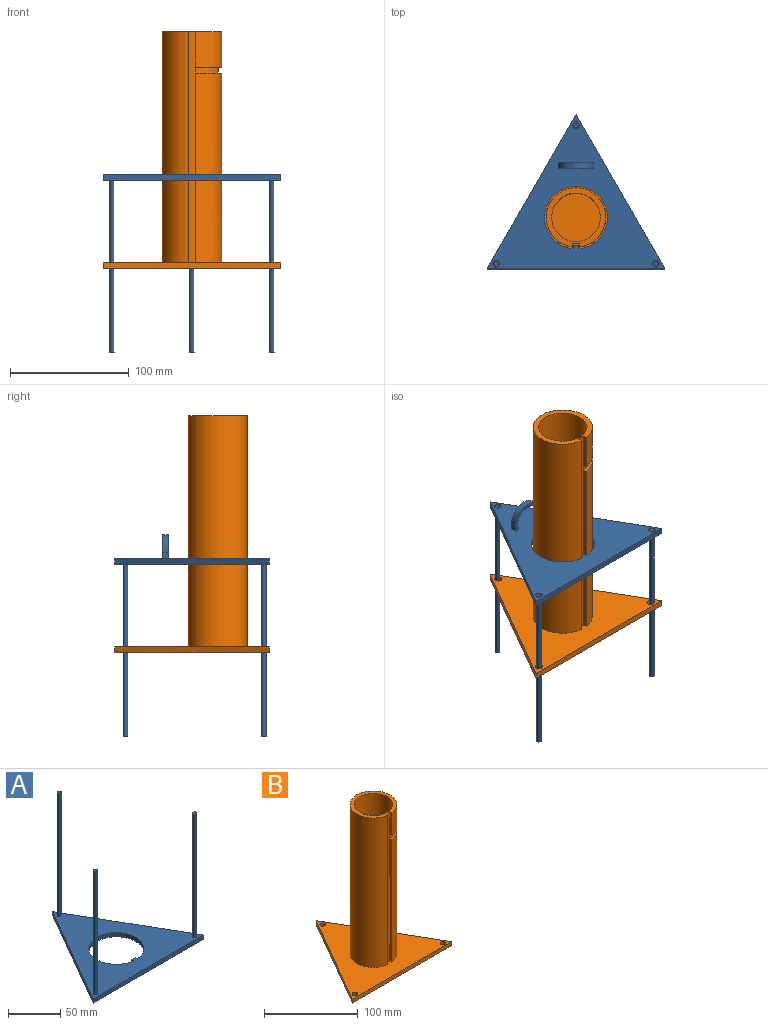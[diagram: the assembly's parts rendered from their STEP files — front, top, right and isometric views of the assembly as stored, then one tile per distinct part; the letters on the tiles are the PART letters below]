
ASSEMBLY  parts=2 mates=2
PART A: 49 faces, bbox 150x129.9x170 mm
  f0: plane 150x129.9mm, normal (0,0,-1), area 7430.6mm2, adj f1,f2,f3,f4,f5,f6,f7,f8
  f1: plane 30x20mm, normal (0,-1,0), area 159mm2, adj f0,f11,f12,f13,f14,f15
  f2: plane 30x20mm, normal (0,1,0), area 159mm2, adj f0,f11,f12,f13,f14,f15
  f3: plane 129.9x75mm, normal (0.87,0.5,0), area 750mm2, adj f0,f4,f8,f10
  f4: plane 129.9x75mm, normal (-0.87,0.5,0), area 750mm2, adj f0,f3,f8,f10
  f5: cylinder r=26.5mm len=53mm, axis (0,0,-1), area 807.5mm2, adj f0,f6,f9,f10
  f6: plane 5x2.7mm, normal (1,0,0), area 13.5mm2, adj f0,f5,f7,f10
  f7: plane 5x5mm, normal (0,1,0), area 25mm2, adj f0,f6,f9,f10
  f8: plane 150x5mm, normal (0,-1,0), area 750mm2, adj f0,f3,f4,f10
  f9: plane 5x2.7mm, normal (-1,0,0), area 13.5mm2, adj f0,f5,f7,f10
  f10: plane 150x129.9mm, normal (0,0,1), area 7512.8mm2, adj f3,f4,f5,f6,f7,f8,f9,f39
  f11: plane 5x5mm, normal (-1,0,0), area 25mm2, adj f0,f1,f2,f15
  f12: plane 5x5mm, normal (1,0,0), area 25mm2, adj f0,f1,f2,f15
  f13: plane 5x5mm, normal (1,0,0), area 25mm2, adj f0,f1,f2,f14
  f14: cylinder r=12mm len=24mm, axis (0,1,0), area 214.3mm2, adj f0,f1,f2,f13
  f15: cylinder r=15mm len=30mm, axis (0,1,0), area 235.6mm2, adj f1,f2,f11,f12
  f16: plane 2.85x2.6mm, normal (0.87,-0.5,0), area 8.6mm2, adj f0,f17,f21,f22
  f17: plane 2.85x2.6mm, normal (0.87,0.5,0), area 8.6mm2, adj f0,f16,f18,f22
  f18: plane 3.29x2.6mm, normal (0,1,0), area 8.6mm2, adj f0,f17,f19,f22
  f19: plane 2.85x2.6mm, normal (-0.87,0.5,0), area 8.6mm2, adj f0,f18,f20,f22
  f20: plane 2.85x2.6mm, normal (-0.87,-0.5,0), area 8.6mm2, adj f0,f19,f21,f22
  f21: plane 3.29x2.6mm, normal (0,-1,0), area 8.6mm2, adj f0,f16,f20,f22
  f22: plane 6.58x5.7mm, normal (0,0,-1), area 15.6mm2, adj f16,f17,f18,f19,f20,f21,f38
  f23: plane 2.85x2.6mm, normal (0.87,-0.5,0), area 8.6mm2, adj f0,f24,f28,f29
  f24: plane 2.85x2.6mm, normal (0.87,0.5,0), area 8.6mm2, adj f0,f23,f25,f29
  f25: plane 3.29x2.6mm, normal (0,1,0), area 8.6mm2, adj f0,f24,f26,f29
  f26: plane 2.85x2.6mm, normal (-0.87,0.5,0), area 8.6mm2, adj f0,f25,f27,f29
  f27: plane 2.85x2.6mm, normal (-0.87,-0.5,0), area 8.6mm2, adj f0,f26,f28,f29
  f28: plane 3.29x2.6mm, normal (0,-1,0), area 8.6mm2, adj f0,f23,f27,f29
  f29: plane 6.58x5.7mm, normal (0,0,-1), area 15.6mm2, adj f23,f24,f25,f26,f27,f28,f46
  f30: plane 2.85x2.6mm, normal (0.87,-0.5,0), area 8.6mm2, adj f0,f31,f35,f36
  f31: plane 2.85x2.6mm, normal (0.87,0.5,0), area 8.6mm2, adj f0,f30,f32,f36
  f32: plane 3.29x2.6mm, normal (0,1,0), area 8.6mm2, adj f0,f31,f33,f36
  f33: plane 2.85x2.6mm, normal (-0.87,0.5,0), area 8.6mm2, adj f0,f32,f34,f36
  f34: plane 2.85x2.6mm, normal (-0.87,-0.5,0), area 8.6mm2, adj f0,f33,f35,f36
  f35: plane 3.29x2.6mm, normal (0,-1,0), area 8.6mm2, adj f0,f30,f34,f36
  f36: plane 6.58x5.7mm, normal (0,0,-1), area 15.6mm2, adj f30,f31,f32,f33,f34,f35,f42
  f37: plane 4x4mm, normal (0,0,-1), area 12.6mm2, adj f38
  f38: cylinder r=2mm len=4mm, axis (0,0,-1), area 32.7mm2, adj f22,f37
  f39: cylinder r=2mm len=145mm, axis (0,0,-1), area 1822.1mm2, adj f10,f40
  f40: plane 4x4mm, normal (0,0,1), area 12.6mm2, adj f39
  f41: plane 4x4mm, normal (0,0,-1), area 12.6mm2, adj f42
  f42: cylinder r=2mm len=4mm, axis (0,0,-1), area 32.7mm2, adj f36,f41
  f43: cylinder r=2mm len=145mm, axis (0,0,-1), area 1822.1mm2, adj f10,f44
  f44: plane 4x4mm, normal (0,0,1), area 12.6mm2, adj f43
  f45: plane 4x4mm, normal (0,0,-1), area 12.6mm2, adj f46
  f46: cylinder r=2mm len=4mm, axis (0,0,-1), area 32.7mm2, adj f29,f45
  f47: cylinder r=2mm len=145mm, axis (0,0,-1), area 1822.1mm2, adj f10,f48
  f48: plane 4x4mm, normal (0,0,1), area 12.6mm2, adj f47
PART B: 25 faces, bbox 150x129.9x200 mm
  f0: plane 35.13x22.19mm, normal (0,0,1), area 131.2mm2, adj f1,f2,f3,f4,f5,f6
  f1: plane 20x2.57mm, normal (-0.51,0.86,0), area 59.7mm2, adj f0,f2,f6,f7
  f2: plane 25x4.72mm, normal (0.86,0.51,0), area 135.6mm2, adj f0,f1,f3,f7,f8,f9,f10
  f3: cylinder r=22mm len=30.85mm, axis (0,0,-1), area 205.2mm2, adj f0,f2,f4,f11
  f4: plane 195x6mm, normal (0,-1,0), area 1169.1mm2, adj f0,f3,f5,f11,f12,f13,f14,f15
  f5: plane 160x3mm, normal (-1,0,0), area 480mm2, adj f0,f4,f6,f15
  f6: cylinder r=25mm len=195mm, axis (0,0,-1), area 28838.8mm2, adj f0,f1,f5,f7,f8,f11,f12,f13
  f7: plane 6.26x5.38mm, normal (0,0,1), area 17mm2, adj f1,f2,f6,f8
  f8: plane 25x2.58mm, normal (0.51,-0.86,0), area 67.2mm2, adj f2,f6,f7,f9,f11
  f9: plane 1.94x1.36mm, normal (0.43,-0.56,-0.71), area 0.4mm2, adj f2,f8,f10,f11
  f10: cone r=17mm half-angle=45deg, axis (0,0,1), area 0.7mm2, adj f2,f9,f11
  f11: plane 39.86x22.19mm, normal (0,0,-1), area 147.5mm2, adj f3,f4,f6,f8,f9,f10,f12
  f12: plane 30x3mm, normal (-1,0,0), area 90mm2, adj f4,f6,f11,f13
  f13: plane 50x49.82mm, normal (0,0,1), area 624.5mm2, adj f4,f6,f12,f14,f16
  f14: plane 195x3mm, normal (1,0,0), area 585mm2, adj f4,f6,f13,f15
  f15: plane 150x129.9mm, normal (0,0,1), area 7713.2mm2, adj f4,f5,f6,f14,f17,f18,f19,f20
  f16: cylinder r=20.5mm len=195mm, axis (0,0,-1), area 25117mm2, adj f13,f23
  f17: cylinder r=3mm len=6mm, axis (0,0,-1), area 94.2mm2, adj f15,f24
  f18: cylinder r=3mm len=6mm, axis (0,0,-1), area 94.2mm2, adj f15,f24
  f19: cylinder r=3mm len=6mm, axis (0,0,-1), area 94.2mm2, adj f15,f24
  f20: plane 129.9x75mm, normal (0.87,0.5,0), area 750mm2, adj f15,f21,f22,f24
  f21: plane 129.9x75mm, normal (-0.87,0.5,0), area 750mm2, adj f15,f20,f22,f24
  f22: plane 150x5mm, normal (0,-1,0), area 750mm2, adj f15,f20,f21,f24
  f23: plane 41x41mm, normal (0,0,1), area 1320.3mm2, adj f16
  f24: plane 150x129.9mm, normal (0,0,-1), area 9658mm2, adj f17,f18,f19,f20,f21,f22
PLACE A rot(axis=(0,1,0),180deg) t=(-148.26,-81.28,107.18)mm
PLACE B t=(-148.26,-81.28,27.64)mm fixed
MATE cylindrical A.f5 <-> B.f6  axis (0,0,1) through (-148.26,-81.28,107.18)mm
MATE slider A.f5 <-> B.f6  axis (0,0,1) through (-148.26,-81.28,107.18)mm
